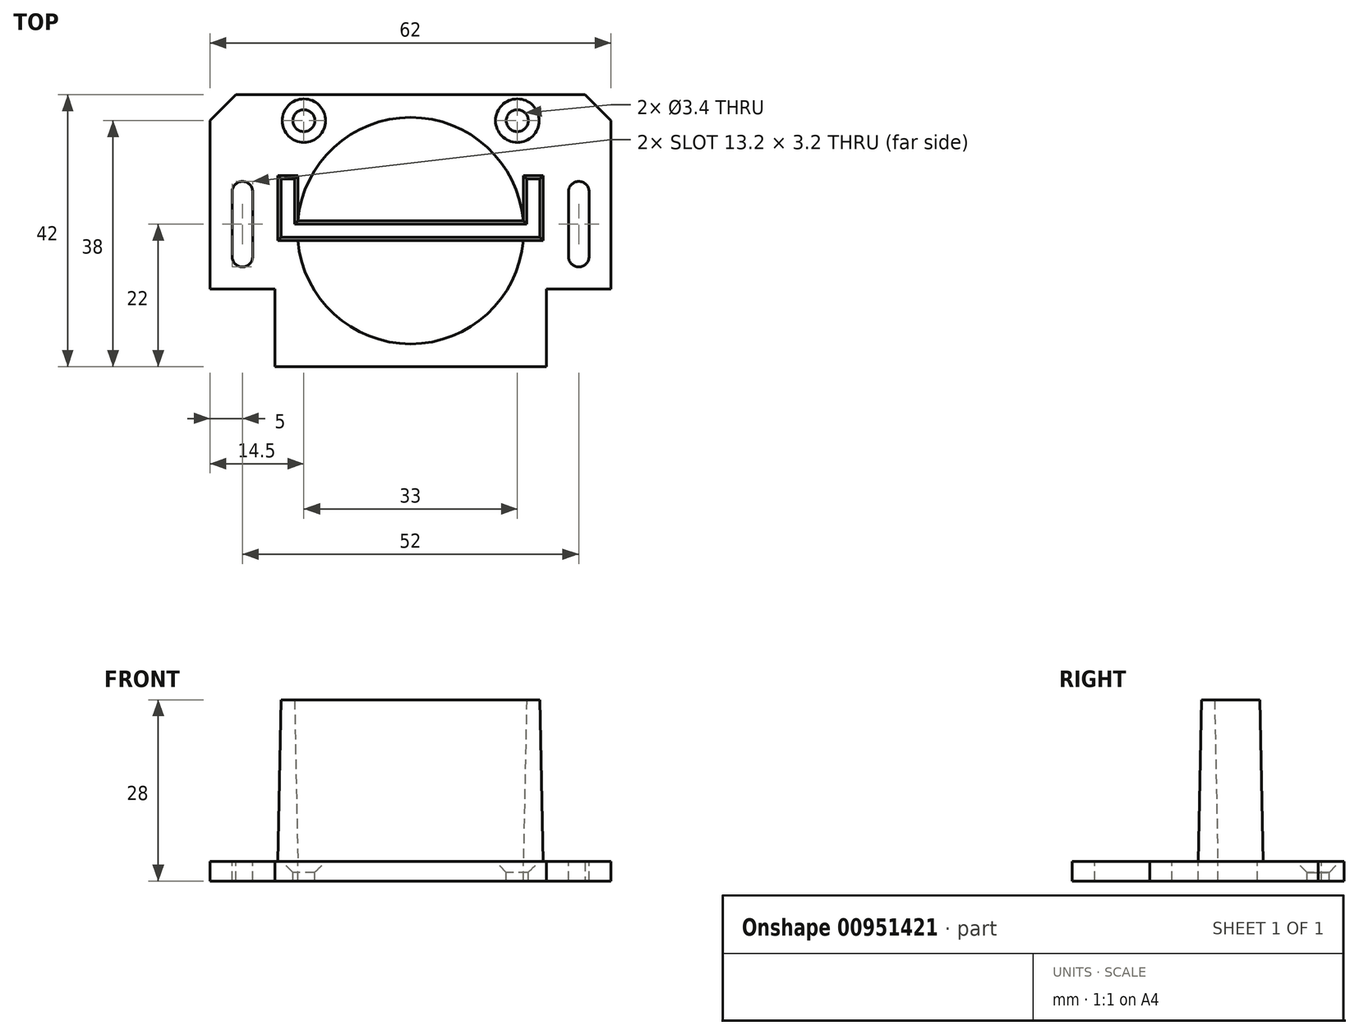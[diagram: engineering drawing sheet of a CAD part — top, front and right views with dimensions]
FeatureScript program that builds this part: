
annotation { "Feature Type Name" : "Feature", "Feature Type Description" : "" }
export const myFeature = defineFeature(function(context is Context, id is Id, definition is map)
    precondition{}
    {
        {
            var Q0;
            Q0=qCreatedBy(makeId("Top.planeOp"),FACE);
            var sketch = newSketch(context, id + "F0", { "sketchPlane" : qUnion([Q0])});
            skArc(sketch, "E0", {"start": v(-17.44, -1.5) * mm, "mid": v(0, -17.5) * mm, "end": v(17.44, -1.5) * mm});
            skLineSegment(sketch, "E1.bottom", {"start": v(-31, 21) * mm, "end": v(31, 21) * mm});
            skLineSegment(sketch, "E1.top", {"start": v(-21, -21) * mm, "end": v(21.02, -21) * mm});
            skLineSegment(sketch, "E1.left", {"start": v(-31, 21) * mm, "end": v(-31, -9) * mm});
            skLineSegment(sketch, "E1.right", {"start": v(31, 21) * mm, "end": v(31, -9) * mm});
            skLineSegment(sketch, "E2", {"start": v(-17.5, 0) * mm, "end": v(17.5, 0) * mm, "construction": true});
            skLineSegment(sketch, "E3.0", {"start": v(-17.44, -1.5) * mm, "end": v(17.44, -1.5) * mm});
            skLineSegment(sketch, "E4.0", {"start": v(-17.44, 1.5) * mm, "end": v(17.44, 1.5) * mm});
            skLineSegment(sketch, "E5.0", {"start": v(26, 21) * mm, "end": v(26, -21) * mm, "construction": true});
            skLineSegment(sketch, "E6.0", {"start": v(-26, 21) * mm, "end": v(-26, -21) * mm, "construction": true});
            skLineSegment(sketch, "E7.bottom", {"start": v(-27.6, -4) * mm, "end": v(-24.4, -4) * mm});
            skLineSegment(sketch, "E7.top", {"start": v(-27.6, 6) * mm, "end": v(-24.4, 6) * mm});
            skLineSegment(sketch, "E7.left", {"start": v(-27.6, -4) * mm, "end": v(-27.6, 6) * mm});
            skLineSegment(sketch, "E7.right", {"start": v(-24.4, -4) * mm, "end": v(-24.4, 6) * mm});
            skPoint(sketch, "E7.middle", {"position": v(-26, 1) * mm});
            skLineSegment(sketch, "E8.bottom", {"start": v(24.4, -4) * mm, "end": v(27.6, -4) * mm, "construction": true});
            skLineSegment(sketch, "E8.top", {"start": v(24.4, 6) * mm, "end": v(27.6, 6) * mm, "construction": true});
            skLineSegment(sketch, "E8.left", {"start": v(24.4, -4) * mm, "end": v(24.4, 6) * mm});
            skLineSegment(sketch, "E8.right", {"start": v(27.6, -4) * mm, "end": v(27.6, 6) * mm});
            skPoint(sketch, "E8.middle", {"position": v(26, 1) * mm});
            skArc(sketch, "E9", {"start": v(27.6, 6) * mm, "mid": v(26, 7.6) * mm, "end": v(24.4, 6) * mm});
            skArc(sketch, "E10", {"start": v(24.4, -4) * mm, "mid": v(26, -5.6) * mm, "end": v(27.6, -4) * mm});
            skArc(sketch, "E11", {"start": v(-27.6, -4) * mm, "mid": v(-26, -5.6) * mm, "end": v(-24.4, -4) * mm});
            skArc(sketch, "E12", {"start": v(-24.4, 6) * mm, "mid": v(-26, 7.6) * mm, "end": v(-27.6, 6) * mm});
            skLineSegment(sketch, "E13", {"start": v(31, -9) * mm, "end": v(21.02, -9) * mm});
            skLineSegment(sketch, "E14", {"start": v(-31, -9) * mm, "end": v(-21, -9) * mm});
            skLineSegment(sketch, "E15", {"start": v(-21, -9) * mm, "end": v(-21, -21) * mm});
            skLineSegment(sketch, "E16", {"start": v(21.02, -9) * mm, "end": v(21.02, -21) * mm});
            skPoint(sketch, "E17.orphan", {"position": v(-31, -21) * mm});
            skPoint(sketch, "E18.trimOffspring.end.orphan", {"position": v(31, -21) * mm});
            skPoint(sketch, "E19", {"position": v(-16.5, 17) * mm});
            skPoint(sketch, "E20", {"position": v(16.5, 17) * mm});
            skLineSegment(sketch, "E21", {"start": v(0, 28) * mm, "end": v(0, -24.83) * mm, "construction": true});
            skArc(sketch, "E22.trimOffspring", {"start": v(17.44, 1.5) * mm, "mid": v(0, 17.5) * mm, "end": v(-17.44, 1.5) * mm});
            skSolve(sketch);
        }
        {
            var Q0;
            Q0=makeQuery(id+"F0.imprint","IMPRINT",FACE,{"disambiguationData":[TD([[makeQuery(id+"F0.imprint","IMPRINT",EDGE,{"derivedFrom":sQuery(id+"F0.wireOp",EDGE,"E0")}),-1.0]])]});
            extrude(context, id + "F1", {"entities" : qUnion([Q0]), "oppositeDirection" : true, "depth" : 3 * mm, "offsetDistance" : 25 * mm});
        }
        {
            var Q0;
            Q0=sQuery(id+"F0.wireOp",VERTEX,"E19");
            var Q1;
            Q1=sQuery(id+"F0.wireOp",VERTEX,"E20");
            var Q2;
            Q2=makeQuery(id+"F1.opExtrude","SWEPT_BODY",BODY,{"disambiguationData":[OSD([sQuery(id+"F0.wireOp",EDGE,"E0"),sQuery(id+"F0.wireOp",EDGE,"E1.bottom"),sQuery(id+"F0.wireOp",EDGE,"E1.top"),sQuery(id+"F0.wireOp",EDGE,"E1.left"),sQuery(id+"F0.wireOp",EDGE,"E1.right"),sQuery(id+"F0.wireOp",EDGE,"E3.0"),sQuery(id+"F0.wireOp",EDGE,"E4.0"),sQuery(id+"F0.wireOp",EDGE,"E7.left"),sQuery(id+"F0.wireOp",EDGE,"E7.right"),sQuery(id+"F0.wireOp",EDGE,"E8.left"),sQuery(id+"F0.wireOp",EDGE,"E8.right"),sQuery(id+"F0.wireOp",EDGE,"E9"),sQuery(id+"F0.wireOp",EDGE,"E10"),sQuery(id+"F0.wireOp",EDGE,"E11"),sQuery(id+"F0.wireOp",EDGE,"E12"),sQuery(id+"F0.wireOp",EDGE,"E13"),sQuery(id+"F0.wireOp",EDGE,"E14"),sQuery(id+"F0.wireOp",EDGE,"E15"),sQuery(id+"F0.wireOp",EDGE,"E16"),sQuery(id+"F0.wireOp",EDGE,"E22.trimOffspring")])]});
            hole(context, id + "F2", {"style" : HoleStyle.C_SINK, "endStyle" : HoleEndStyle.THROUGH, "standardTappedOrClearance" : lookupTablePath({ "fit" : "Normal", "standard" : "ISO", "size" : "M3", "type" : "Clearance" }), "standardBlindInLast" : lookupTablePath({ "fit" : "Normal", "standard" : "ISO", "engagement" : "75%", "pitch" : "0.5 mm", "size" : "M3", "type" : "Clearance & tapped" }), "holeDiameter" : 3.4 * mm, "cSinkDiameter" : 6.72 * mm, "cSinkAngle" : 90 * degree, "majorDiameter" : 5 * mm, "isTappedThrough" : true, "tappedDepth" : 12 * mm, "tapClearance" : 3, "locations" : qUnion([Q0, Q1]), "scope" : qUnion([Q2])});
        }
        {
            var Q0;
            Q0=makeQuery(id+"F1.opExtrude","SWEPT_EDGE",EDGE,{"disambiguationData":[OSD([sQuery(id+"F0.wireOp",EDGE,"E1.bottom"),sQuery(id+"F0.wireOp",EDGE,"E1.right")])]});
            var Q1;
            Q1=makeQuery(id+"F1.opExtrude","SWEPT_EDGE",EDGE,{"disambiguationData":[OSD([sQuery(id+"F0.wireOp",EDGE,"E1.bottom"),sQuery(id+"F0.wireOp",EDGE,"E1.left")])]});
            chamfer(context, id + "F3", {"entities" : qUnion([Q0, Q1]), "width" : 4 * mm, "tangentPropagation" : true});
        }
        {
            var Q0;
            Q0=makeQuery(id+"F1.opExtrude","CAP_FACE",FACE,{"disambiguationData":[OSD([sQuery(id+"F0.wireOp",EDGE,"E0"),sQuery(id+"F0.wireOp",EDGE,"E1.bottom"),sQuery(id+"F0.wireOp",EDGE,"E1.top"),sQuery(id+"F0.wireOp",EDGE,"E1.left"),sQuery(id+"F0.wireOp",EDGE,"E1.right"),sQuery(id+"F0.wireOp",EDGE,"E3.0"),sQuery(id+"F0.wireOp",EDGE,"E4.0"),sQuery(id+"F0.wireOp",EDGE,"E7.left"),sQuery(id+"F0.wireOp",EDGE,"E7.right"),sQuery(id+"F0.wireOp",EDGE,"E8.left"),sQuery(id+"F0.wireOp",EDGE,"E8.right"),sQuery(id+"F0.wireOp",EDGE,"E9"),sQuery(id+"F0.wireOp",EDGE,"E10"),sQuery(id+"F0.wireOp",EDGE,"E11"),sQuery(id+"F0.wireOp",EDGE,"E12"),sQuery(id+"F0.wireOp",EDGE,"E13"),sQuery(id+"F0.wireOp",EDGE,"E14"),sQuery(id+"F0.wireOp",EDGE,"E15"),sQuery(id+"F0.wireOp",EDGE,"E16"),sQuery(id+"F0.wireOp",EDGE,"E22.trimOffspring")])],"isStart":true});
            var sketch = newSketch(context, id + "F4", { "sketchPlane" : qUnion([Q0])});
            skLineSegment(sketch, "E23.0", {"start": v(-17.44, 1.5) * mm, "end": v(17.44, 1.5) * mm});
            skLineSegment(sketch, "E24.0", {"start": v(-17.44, -1.5) * mm, "end": v(17.44, -1.5) * mm});
            skLineSegment(sketch, "E25", {"start": v(-20.5, -1.5) * mm, "end": v(-20.5, 8.5) * mm});
            skLineSegment(sketch, "E26", {"start": v(20.5, -1.5) * mm, "end": v(20.5, 8.5) * mm});
            skLineSegment(sketch, "E27", {"start": v(-17.44, -1.5) * mm, "end": v(-20.5, -1.5) * mm});
            skLineSegment(sketch, "E28", {"start": v(17.44, -1.5) * mm, "end": v(20.5, -1.5) * mm});
            skLineSegment(sketch, "E29", {"start": v(-20.5, 8.5) * mm, "end": v(-17.44, 8.5) * mm});
            skLineSegment(sketch, "E30", {"start": v(-17.44, 8.5) * mm, "end": v(-17.44, 1.5) * mm});
            skLineSegment(sketch, "E31", {"start": v(17.44, 1.5) * mm, "end": v(17.44, 8.5) * mm});
            skLineSegment(sketch, "E32", {"start": v(17.44, 8.5) * mm, "end": v(20.5, 8.5) * mm});
            skLineSegment(sketch, "E33.0.0", {"start": v(27, 21) * mm, "end": v(-27, 21) * mm});
            skLineSegment(sketch, "E33.0.1", {"start": v(-27, 21) * mm, "end": v(-31, 17) * mm});
            skLineSegment(sketch, "E33.0.2", {"start": v(-31, 17) * mm, "end": v(-31, -9) * mm});
            skLineSegment(sketch, "E33.0.3", {"start": v(-31, -9) * mm, "end": v(-21, -9) * mm});
            skLineSegment(sketch, "E33.0.4", {"start": v(-21, -9) * mm, "end": v(-21, -21) * mm});
            skLineSegment(sketch, "E33.0.5", {"start": v(-21, -21) * mm, "end": v(21.02, -21) * mm});
            skLineSegment(sketch, "E33.0.6", {"start": v(21.02, -21) * mm, "end": v(21.02, -9) * mm});
            skLineSegment(sketch, "E33.0.7", {"start": v(21.02, -9) * mm, "end": v(31, -9) * mm});
            skLineSegment(sketch, "E33.0.8", {"start": v(31, -9) * mm, "end": v(31, 17) * mm});
            skLineSegment(sketch, "E33.0.9", {"start": v(31, 17) * mm, "end": v(27, 21) * mm});
            skSolve(sketch);
        }
        {
            var Q0;
            Q0=makeQuery(id+"F4.imprint","IMPRINT",FACE,{"disambiguationData":[TD([[makeQuery(id+"F4.imprint","IMPRINT",EDGE,{"derivedFrom":sQuery(id+"F4.wireOp",EDGE,"E25")}),1.0]])]});
            cPlane(context, id + "F5", {"entities" : qUnion([Q0]), "cplaneType" : CPlaneType.OFFSET, "offset" : 25 * mm, "width" : 150 * mm, "height" : 150 * mm});
        }
        {
            var Q0;
            Q0=qCreatedBy(id+"F5.planeOp",FACE);
            var sketch = newSketch(context, id + "F6", { "sketchPlane" : qUnion([Q0])});
            skLineSegment(sketch, "E34.0", {"start": v(-17.94, 8) * mm, "end": v(-17.94, 1) * mm});
            skLineSegment(sketch, "E34.1", {"start": v(-20, 8) * mm, "end": v(-17.94, 8) * mm});
            skLineSegment(sketch, "E34.2", {"start": v(-17.94, 1) * mm, "end": v(17.94, 1) * mm});
            skLineSegment(sketch, "E34.3", {"start": v(-20, -1) * mm, "end": v(-20, 8) * mm});
            skLineSegment(sketch, "E34.4", {"start": v(-17.44, -1) * mm, "end": v(-20, -1) * mm});
            skLineSegment(sketch, "E34.5", {"start": v(-17.44, -1) * mm, "end": v(17.44, -1) * mm});
            skLineSegment(sketch, "E34.6", {"start": v(17.94, 1) * mm, "end": v(17.94, 8) * mm});
            skLineSegment(sketch, "E34.7", {"start": v(17.94, 8) * mm, "end": v(20, 8) * mm});
            skLineSegment(sketch, "E34.8", {"start": v(20, -1) * mm, "end": v(20, 8) * mm});
            skLineSegment(sketch, "E34.9", {"start": v(17.44, -1) * mm, "end": v(20, -1) * mm});
            skSolve(sketch);
        }
        {
            var Q1;
            Q1=qSketchRegion(id+"F6",true);
            var Q2;
            Q2=makeQuery(id+"F4.imprint","IMPRINT",FACE,{"disambiguationData":[TD([[makeQuery(id+"F4.imprint","IMPRINT",EDGE,{"derivedFrom":sQuery(id+"F4.wireOp",EDGE,"E23.0")}),-1.0]])]});
            loft(context, id + "F7", {"operationType" : NewBodyOperationType.ADD, "sheetProfilesArray" : [{ "sheetProfileEntities" : qUnion([Q1]) }, { "sheetProfileEntities" : qUnion([Q2]) }]});
        }
    });
